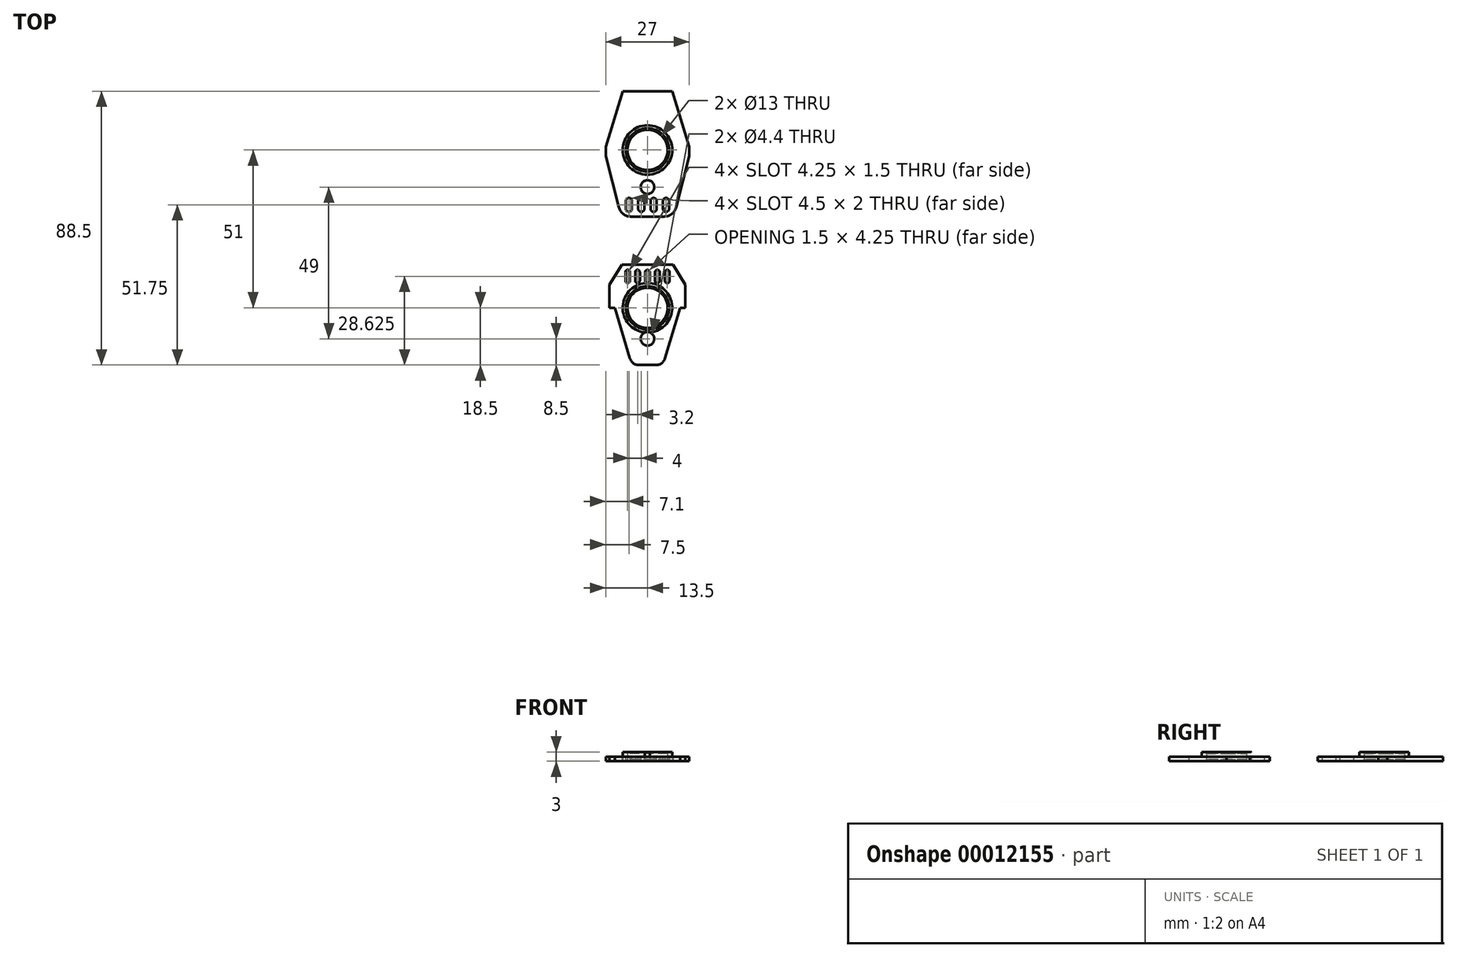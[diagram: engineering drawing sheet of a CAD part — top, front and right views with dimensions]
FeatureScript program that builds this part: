
annotation { "Feature Type Name" : "Feature", "Feature Type Description" : "" }
export const myFeature = defineFeature(function(context is Context, id is Id, definition is map)
    precondition{}
    {
        {
            var Q0;
            Q0=qCreatedBy(makeId("Top.planeOp"),FACE);
            var sketch = newSketch(context, id + "F0", { "sketchPlane" : qUnion([Q0])});
            skLineSegment(sketch, "E0", {"start": v(-13.5, 0) * mm, "end": v(-9.27, -16.5) * mm});
            skLineSegment(sketch, "E1", {"start": v(-5.4, -19.5) * mm, "end": v(0, -19.5) * mm});
            skLineSegment(sketch, "E2", {"start": v(0, -19.5) * mm, "end": v(0, 21) * mm, "construction": true});
            skLineSegment(sketch, "E3", {"start": v(0, 21) * mm, "end": v(-8, 21) * mm});
            skLineSegment(sketch, "E4", {"start": v(-13.5, 0) * mm, "end": v(-13.5, 3) * mm});
            skLineSegment(sketch, "E5", {"start": v(-13.5, 3) * mm, "end": v(-8, 21) * mm});
            skPoint(sketch, "E6.visualSharp", {"position": v(-8.5, -19.5) * mm});
            skArc(sketch, "E6.filletArc", {"start": v(-9.27, -16.5) * mm, "mid": v(-7.85, -18.66) * mm, "end": v(-5.4, -19.5) * mm});
            skLineSegment(sketch, "E7.0.MirrorCS", {"start": v(13.5, 0) * mm, "end": v(13.5, 3) * mm});
            skArc(sketch, "E7.1.MirrorCS", {"start": v(9.27, -16.5) * mm, "mid": v(7.85, -18.66) * mm, "end": v(5.4, -19.5) * mm});
            skPoint(sketch, "E7.2.MirrorP", {"position": v(8.5, -19.5) * mm});
            skLineSegment(sketch, "E7.3.MirrorCS", {"start": v(13.5, 3) * mm, "end": v(8, 21) * mm});
            skLineSegment(sketch, "E7.4.MirrorCS", {"start": v(0, 21) * mm, "end": v(8, 21) * mm});
            skLineSegment(sketch, "E7.5.MirrorCS", {"start": v(13.5, 0) * mm, "end": v(9.27, -16.5) * mm});
            skLineSegment(sketch, "E7.6.MirrorCS", {"start": v(5.4, -19.5) * mm, "end": v(0, -19.5) * mm});
            skSolve(sketch);
        }
        {
            var Q0;
            Q0 = qSketchRegion(id + "F0", true);
            extrude(context, id + "F1", {"entities" : qUnion([Q0]), "depth" : 1.5 * mm});
        }
        {
            var Q0;
            Q0=makeQuery(id+"F1.opExtrude","CAP_FACE",FACE,{"disambiguationData":[OSD([sQuery(id+"F0.wireOp",EDGE,"E0"),sQuery(id+"F0.wireOp",EDGE,"E1"),sQuery(id+"F0.wireOp",EDGE,"E3"),sQuery(id+"F0.wireOp",EDGE,"E4"),sQuery(id+"F0.wireOp",EDGE,"E5"),sQuery(id+"F0.wireOp",EDGE,"E6.filletArc"),sQuery(id+"F0.wireOp",EDGE,"E7.0.MirrorCS"),sQuery(id+"F0.wireOp",EDGE,"E7.1.MirrorCS"),sQuery(id+"F0.wireOp",EDGE,"E7.3.MirrorCS"),sQuery(id+"F0.wireOp",EDGE,"E7.4.MirrorCS"),sQuery(id+"F0.wireOp",EDGE,"E7.5.MirrorCS"),sQuery(id+"F0.wireOp",EDGE,"E7.6.MirrorCS")])],"isStart":false});
            var sketch = newSketch(context, id + "F2", { "sketchPlane" : qUnion([Q0])});
            skCircle(sketch, "E8", {"center": v(0, 2) * mm, "radius": 8 * mm});
            skCircle(sketch, "E9", {"center": v(0, 2) * mm, "radius": 6.5 * mm});
            skSolve(sketch);
        }
        {
            var Q0;
            Q0 = qSketchRegion(id + "F2", true);
            extrude(context, id + "F3", {"entities" : qUnion([Q0]), "operationType" : NewBodyOperationType.ADD, "depth" : 1.5 * mm});
        }
        {
            var Q0;
            Q0=makeQuery(id+"F1.opExtrude","CAP_FACE",FACE,{"disambiguationData":[OSD([sQuery(id+"F0.wireOp",EDGE,"E0"),sQuery(id+"F0.wireOp",EDGE,"E1"),sQuery(id+"F0.wireOp",EDGE,"E3"),sQuery(id+"F0.wireOp",EDGE,"E4"),sQuery(id+"F0.wireOp",EDGE,"E5"),sQuery(id+"F0.wireOp",EDGE,"E6.filletArc"),sQuery(id+"F0.wireOp",EDGE,"E7.0.MirrorCS"),sQuery(id+"F0.wireOp",EDGE,"E7.1.MirrorCS"),sQuery(id+"F0.wireOp",EDGE,"E7.3.MirrorCS"),sQuery(id+"F0.wireOp",EDGE,"E7.4.MirrorCS"),sQuery(id+"F0.wireOp",EDGE,"E7.5.MirrorCS"),sQuery(id+"F0.wireOp",EDGE,"E7.6.MirrorCS")])],"isStart":false});
            var sketch = newSketch(context, id + "F4", { "sketchPlane" : qUnion([Q0])});
            skCircle(sketch, "E10", {"center": v(0, 2) * mm, "radius": 6.5 * mm});
            skCircle(sketch, "E11", {"center": v(0, -10) * mm, "radius": 2.2 * mm});
            skLineSegment(sketch, "E12", {"start": v(-7, -14.5) * mm, "end": v(-7, -17) * mm});
            skArc(sketch, "E13", {"start": v(-7, -17) * mm, "mid": v(-6, -18) * mm, "end": v(-5, -17) * mm});
            skLineSegment(sketch, "E14", {"start": v(-5, -17) * mm, "end": v(-5, -14.5) * mm});
            skArc(sketch, "E15", {"start": v(-5, -14.5) * mm, "mid": v(-6, -13.5) * mm, "end": v(-7, -14.5) * mm});
            skArc(sketch, "E16.1.0.0", {"start": v(-3, -17) * mm, "mid": v(-2, -18) * mm, "end": v(-1, -17) * mm});
            skLineSegment(sketch, "E16.1.0.1", {"start": v(-1, -17) * mm, "end": v(-1, -14.5) * mm});
            skArc(sketch, "E16.1.0.2", {"start": v(-1, -14.5) * mm, "mid": v(-2, -13.5) * mm, "end": v(-3, -14.5) * mm});
            skLineSegment(sketch, "E16.1.0.3", {"start": v(-3, -14.5) * mm, "end": v(-3, -17) * mm});
            skArc(sketch, "E16.2.0.0", {"start": v(1, -17) * mm, "mid": v(2, -18) * mm, "end": v(3, -17) * mm});
            skLineSegment(sketch, "E16.2.0.1", {"start": v(3, -17) * mm, "end": v(3, -14.5) * mm});
            skArc(sketch, "E16.2.0.2", {"start": v(3, -14.5) * mm, "mid": v(2, -13.5) * mm, "end": v(1, -14.5) * mm});
            skLineSegment(sketch, "E16.2.0.3", {"start": v(1, -14.5) * mm, "end": v(1, -17) * mm});
            skArc(sketch, "E16.3.0.0", {"start": v(5, -17) * mm, "mid": v(6, -18) * mm, "end": v(7, -17) * mm});
            skLineSegment(sketch, "E16.3.0.1", {"start": v(7, -17) * mm, "end": v(7, -14.5) * mm});
            skArc(sketch, "E16.3.0.2", {"start": v(7, -14.5) * mm, "mid": v(6, -13.5) * mm, "end": v(5, -14.5) * mm});
            skLineSegment(sketch, "E16.3.0.3", {"start": v(5, -14.5) * mm, "end": v(5, -17) * mm});
            skLineSegment(sketch, "E16.direction1", {"start": v(-7, -17) * mm, "end": v(-3, -17) * mm, "construction": true});
            skSolve(sketch);
        }
        {
            var Q0;
            Q0 = qSketchRegion(id + "F4", true);
            extrude(context, id + "F5", {"entities" : qUnion([Q0]), "operationType" : NewBodyOperationType.REMOVE, "endBound" : BoundingType.THROUGH_ALL, "oppositeDirection" : true, "depth" : 25 * mm});
        }
        {
            var Q0;
            Q0=qCreatedBy(makeId("Top.planeOp"),FACE);
            var sketch = newSketch(context, id + "F6", { "sketchPlane" : qUnion([Q0])});
            skLineSegment(sketch, "E17", {"start": v(0, -35) * mm, "end": v(0, -67.5) * mm, "construction": true});
            skLineSegment(sketch, "E18", {"start": v(0, -67.5) * mm, "end": v(-2.76, -67.5) * mm});
            skLineSegment(sketch, "E19", {"start": v(-5.64, -65.35) * mm, "end": v(-10.5, -49) * mm});
            skLineSegment(sketch, "E20", {"start": v(-10.5, -49) * mm, "end": v(-12.25, -49) * mm});
            skLineSegment(sketch, "E21", {"start": v(-12.25, -49) * mm, "end": v(-12.25, -41.5) * mm});
            skLineSegment(sketch, "E22", {"start": v(-12.25, -41.5) * mm, "end": v(-8.25, -35) * mm});
            skLineSegment(sketch, "E23", {"start": v(-8.25, -35) * mm, "end": v(0, -35) * mm});
            skPoint(sketch, "E24.visualSharp", {"position": v(-5, -67.5) * mm});
            skArc(sketch, "E24.filletArc", {"start": v(-5.64, -65.35) * mm, "mid": v(-4.56, -66.9) * mm, "end": v(-2.76, -67.5) * mm});
            skLineSegment(sketch, "E25.0.MirrorCS", {"start": v(12.25, -41.5) * mm, "end": v(8.25, -35) * mm});
            skLineSegment(sketch, "E25.1.MirrorCS", {"start": v(12.25, -49) * mm, "end": v(12.25, -41.5) * mm});
            skLineSegment(sketch, "E25.2.MirrorCS", {"start": v(0, -67.5) * mm, "end": v(2.76, -67.5) * mm});
            skPoint(sketch, "E25.3.MirrorP", {"position": v(5, -67.5) * mm});
            skLineSegment(sketch, "E25.4.MirrorCS", {"start": v(10.5, -49) * mm, "end": v(12.25, -49) * mm});
            skArc(sketch, "E25.5.MirrorCS", {"start": v(5.64, -65.35) * mm, "mid": v(4.56, -66.9) * mm, "end": v(2.76, -67.5) * mm});
            skLineSegment(sketch, "E25.6.MirrorCS", {"start": v(5.64, -65.35) * mm, "end": v(10.5, -49) * mm});
            skLineSegment(sketch, "E25.7.MirrorCS", {"start": v(8.25, -35) * mm, "end": v(0, -35) * mm});
            skSolve(sketch);
        }
        {
            var Q0;
            Q0 = qSketchRegion(id + "F6", true);
            extrude(context, id + "F7", {"entities" : qUnion([Q0]), "depth" : 1.5 * mm});
        }
        {
            var Q0;
            Q0=makeQuery(id+"F7.opExtrude","CAP_FACE",FACE,{"disambiguationData":[OSD([sQuery(id+"F6.wireOp",EDGE,"E18"),sQuery(id+"F6.wireOp",EDGE,"E19"),sQuery(id+"F6.wireOp",EDGE,"E20"),sQuery(id+"F6.wireOp",EDGE,"E21"),sQuery(id+"F6.wireOp",EDGE,"E22"),sQuery(id+"F6.wireOp",EDGE,"E23"),sQuery(id+"F6.wireOp",EDGE,"E24.filletArc"),sQuery(id+"F6.wireOp",EDGE,"E25.0.MirrorCS"),sQuery(id+"F6.wireOp",EDGE,"E25.1.MirrorCS"),sQuery(id+"F6.wireOp",EDGE,"E25.2.MirrorCS"),sQuery(id+"F6.wireOp",EDGE,"E25.4.MirrorCS"),sQuery(id+"F6.wireOp",EDGE,"E25.5.MirrorCS"),sQuery(id+"F6.wireOp",EDGE,"E25.6.MirrorCS"),sQuery(id+"F6.wireOp",EDGE,"E25.7.MirrorCS")])],"isStart":false});
            var sketch = newSketch(context, id + "F8", { "sketchPlane" : qUnion([Q0])});
            skCircle(sketch, "E26", {"center": v(0, -49) * mm, "radius": 6.5 * mm});
            skCircle(sketch, "E27", {"center": v(0, -49) * mm, "radius": 8 * mm});
            skSolve(sketch);
        }
        {
            var Q0;
            Q0 = qSketchRegion(id + "F8", true);
            extrude(context, id + "F9", {"entities" : qUnion([Q0]), "operationType" : NewBodyOperationType.ADD, "depth" : 1.5 * mm});
        }
        {
            var Q0;
            Q0=makeQuery(id+"F9.boolean.opBoolean","SPLIT",FACE,{"disambiguationData":[TD([makeQuery(id+"F9.opExtrude","SWEPT_FACE",FACE,{"disambiguationData":[OSD([sQuery(id+"F8.wireOp",EDGE,"E26")])]})])],"derivedFrom":makeQuery(id+"F7.opExtrude","CAP_FACE",FACE,{"disambiguationData":[OSD([sQuery(id+"F6.wireOp",EDGE,"E18"),sQuery(id+"F6.wireOp",EDGE,"E19"),sQuery(id+"F6.wireOp",EDGE,"E20"),sQuery(id+"F6.wireOp",EDGE,"E21"),sQuery(id+"F6.wireOp",EDGE,"E22"),sQuery(id+"F6.wireOp",EDGE,"E23"),sQuery(id+"F6.wireOp",EDGE,"E24.filletArc"),sQuery(id+"F6.wireOp",EDGE,"E25.0.MirrorCS"),sQuery(id+"F6.wireOp",EDGE,"E25.1.MirrorCS"),sQuery(id+"F6.wireOp",EDGE,"E25.2.MirrorCS"),sQuery(id+"F6.wireOp",EDGE,"E25.4.MirrorCS"),sQuery(id+"F6.wireOp",EDGE,"E25.5.MirrorCS"),sQuery(id+"F6.wireOp",EDGE,"E25.6.MirrorCS"),sQuery(id+"F6.wireOp",EDGE,"E25.7.MirrorCS")])],"isStart":false})});
            var sketch = newSketch(context, id + "F10", { "sketchPlane" : qUnion([Q0])});
            skCircle(sketch, "E28", {"center": v(0, -49) * mm, "radius": 6.5 * mm});
            skSolve(sketch);
        }
        {
            var Q0;
            Q0 = qSketchRegion(id + "F10", true);
            extrude(context, id + "F11", {"entities" : qUnion([Q0]), "operationType" : NewBodyOperationType.REMOVE, "endBound" : BoundingType.THROUGH_ALL, "oppositeDirection" : true, "depth" : 25 * mm});
        }
        {
            var Q0;
            {var subQ0=sQuery(id+"F6.wireOp",EDGE,"E18");var subQ1=sQuery(id+"F6.wireOp",EDGE,"E19");var subQ2=sQuery(id+"F6.wireOp",EDGE,"E20");var subQ3=sQuery(id+"F6.wireOp",EDGE,"E21");var subQ4=sQuery(id+"F6.wireOp",EDGE,"E22");var subQ5=sQuery(id+"F6.wireOp",EDGE,"E23");var subQ6=sQuery(id+"F6.wireOp",EDGE,"E24.filletArc");var subQ7=sQuery(id+"F6.wireOp",EDGE,"E25.0.MirrorCS");var subQ8=sQuery(id+"F6.wireOp",EDGE,"E25.1.MirrorCS");var subQ9=sQuery(id+"F6.wireOp",EDGE,"E25.2.MirrorCS");var subQ10=sQuery(id+"F6.wireOp",EDGE,"E25.4.MirrorCS");var subQ11=sQuery(id+"F6.wireOp",EDGE,"E25.5.MirrorCS");var subQ12=sQuery(id+"F6.wireOp",EDGE,"E25.6.MirrorCS");var subQ13=sQuery(id+"F6.wireOp",EDGE,"E25.7.MirrorCS");Q0=makeQuery(id+"F9.boolean.opBoolean","SPLIT",FACE,{"disambiguationData":[TD([makeQuery(id+"F7.opExtrude","SWEPT_FACE",FACE,{"disambiguationData":[OSD([subQ1])]})])],"derivedFrom":makeQuery(id+"F7.opExtrude","CAP_FACE",FACE,{"disambiguationData":[OSD([subQ0,subQ1,subQ2,subQ3,subQ4,subQ5,subQ6,subQ7,subQ8,subQ9,subQ10,subQ11,subQ12,subQ13])],"isStart":false})});}
            var sketch = newSketch(context, id + "F12", { "sketchPlane" : qUnion([Q0])});
            skLineSegment(sketch, "E29", {"start": v(-0.75, -37.5) * mm, "end": v(-0.75, -40.25) * mm});
            skArc(sketch, "E30", {"start": v(-0.75, -40.25) * mm, "mid": v(0, -41) * mm, "end": v(0.75, -40.25) * mm});
            skLineSegment(sketch, "E31", {"start": v(0.75, -40.25) * mm, "end": v(0.75, -37.5) * mm});
            skArc(sketch, "E32", {"start": v(0.75, -37.5) * mm, "mid": v(0, -36.75) * mm, "end": v(-0.75, -37.5) * mm});
            skArc(sketch, "E33.1.0.0", {"start": v(3.95, -37.5) * mm, "mid": v(3.2, -36.75) * mm, "end": v(2.45, -37.5) * mm});
            skLineSegment(sketch, "E33.1.0.1", {"start": v(3.95, -40.25) * mm, "end": v(3.95, -37.5) * mm});
            skLineSegment(sketch, "E33.1.0.2", {"start": v(2.45, -37.5) * mm, "end": v(2.45, -40.25) * mm});
            skArc(sketch, "E33.1.0.3", {"start": v(2.45, -40.25) * mm, "mid": v(3.2, -41) * mm, "end": v(3.95, -40.25) * mm});
            skArc(sketch, "E33.2.0.0", {"start": v(7.15, -37.5) * mm, "mid": v(6.4, -36.75) * mm, "end": v(5.65, -37.5) * mm});
            skLineSegment(sketch, "E33.2.0.1", {"start": v(7.15, -40.25) * mm, "end": v(7.15, -37.5) * mm});
            skLineSegment(sketch, "E33.2.0.2", {"start": v(5.65, -37.5) * mm, "end": v(5.65, -40.25) * mm});
            skArc(sketch, "E33.2.0.3", {"start": v(5.65, -40.25) * mm, "mid": v(6.4, -41) * mm, "end": v(7.15, -40.25) * mm});
            skLineSegment(sketch, "E33.direction1", {"start": v(-0.75, -37.5) * mm, "end": v(2.45, -37.5) * mm, "construction": true});
            skArc(sketch, "E34.1.0.0", {"start": v(-3.95, -40.25) * mm, "mid": v(-3.2, -41) * mm, "end": v(-2.45, -40.25) * mm});
            skLineSegment(sketch, "E34.1.0.1", {"start": v(-3.95, -37.5) * mm, "end": v(-3.95, -40.25) * mm});
            skArc(sketch, "E34.1.0.2", {"start": v(-2.45, -37.5) * mm, "mid": v(-3.2, -36.75) * mm, "end": v(-3.95, -37.5) * mm});
            skLineSegment(sketch, "E34.1.0.3", {"start": v(-2.45, -40.25) * mm, "end": v(-2.45, -37.5) * mm});
            skArc(sketch, "E34.2.0.0", {"start": v(-7.15, -40.25) * mm, "mid": v(-6.4, -41) * mm, "end": v(-5.65, -40.25) * mm});
            skLineSegment(sketch, "E34.2.0.1", {"start": v(-7.15, -37.5) * mm, "end": v(-7.15, -40.25) * mm});
            skArc(sketch, "E34.2.0.2", {"start": v(-5.65, -37.5) * mm, "mid": v(-6.4, -36.75) * mm, "end": v(-7.15, -37.5) * mm});
            skLineSegment(sketch, "E34.2.0.3", {"start": v(-5.65, -40.25) * mm, "end": v(-5.65, -37.5) * mm});
            skLineSegment(sketch, "E34.direction1", {"start": v(-0.75, -40.25) * mm, "end": v(-3.95, -40.25) * mm, "construction": true});
            skCircle(sketch, "E35", {"center": v(0, -59) * mm, "radius": 2.2 * mm});
            skSolve(sketch);
        }
        {
            var Q0;
            Q0 = qSketchRegion(id + "F12", true);
            extrude(context, id + "F13", {"entities" : qUnion([Q0]), "operationType" : NewBodyOperationType.REMOVE, "endBound" : BoundingType.THROUGH_ALL, "depth" : 25 * mm, "hasSecondDirection" : true, "secondDirectionBound" : SecondDirectionBoundingType.THROUGH_ALL, "secondDirectionOppositeDirection" : true, "secondDirectionDepth" : 25 * mm});
        }
        {
            var Q0;
            Q0=makeQuery(id+"F3.opExtrude","CAP_EDGE",EDGE,{"disambiguationData":[OSD([sQuery(id+"F2.wireOp",EDGE,"E9")])],"isStart":false});
            var Q1;
            Q1=makeQuery(id+"F5.boolean.opBoolean","INTERSECT",EDGE,{"derivedFrom":[makeQuery(id+"F1.opExtrude","CAP_FACE",FACE,{"disambiguationData":[OSD([sQuery(id+"F0.wireOp",EDGE,"E0"),sQuery(id+"F0.wireOp",EDGE,"E1"),sQuery(id+"F0.wireOp",EDGE,"E3"),sQuery(id+"F0.wireOp",EDGE,"E4"),sQuery(id+"F0.wireOp",EDGE,"E5"),sQuery(id+"F0.wireOp",EDGE,"E6.filletArc"),sQuery(id+"F0.wireOp",EDGE,"E7.0.MirrorCS"),sQuery(id+"F0.wireOp",EDGE,"E7.1.MirrorCS"),sQuery(id+"F0.wireOp",EDGE,"E7.3.MirrorCS"),sQuery(id+"F0.wireOp",EDGE,"E7.4.MirrorCS"),sQuery(id+"F0.wireOp",EDGE,"E7.5.MirrorCS"),sQuery(id+"F0.wireOp",EDGE,"E7.6.MirrorCS")])],"isStart":true}),makeQuery(id+"F5.opExtrude","SWEPT_FACE",FACE,{"disambiguationData":[OSD([sQuery(id+"F4.wireOp",EDGE,"E10")])]})]});
            var Q2;
            Q2=makeQuery(id+"F9.opExtrude","CAP_EDGE",EDGE,{"disambiguationData":[OSD([sQuery(id+"F8.wireOp",EDGE,"E26")])],"isStart":false});
            var Q3;
            Q3=makeQuery(id+"F11.boolean.opBoolean","INTERSECT",EDGE,{"derivedFrom":[makeQuery(id+"F7.opExtrude","CAP_FACE",FACE,{"disambiguationData":[OSD([sQuery(id+"F6.wireOp",EDGE,"E18"),sQuery(id+"F6.wireOp",EDGE,"E19"),sQuery(id+"F6.wireOp",EDGE,"E20"),sQuery(id+"F6.wireOp",EDGE,"E21"),sQuery(id+"F6.wireOp",EDGE,"E22"),sQuery(id+"F6.wireOp",EDGE,"E23"),sQuery(id+"F6.wireOp",EDGE,"E24.filletArc"),sQuery(id+"F6.wireOp",EDGE,"E25.0.MirrorCS"),sQuery(id+"F6.wireOp",EDGE,"E25.1.MirrorCS"),sQuery(id+"F6.wireOp",EDGE,"E25.2.MirrorCS"),sQuery(id+"F6.wireOp",EDGE,"E25.4.MirrorCS"),sQuery(id+"F6.wireOp",EDGE,"E25.5.MirrorCS"),sQuery(id+"F6.wireOp",EDGE,"E25.6.MirrorCS"),sQuery(id+"F6.wireOp",EDGE,"E25.7.MirrorCS")])],"isStart":true}),makeQuery(id+"F11.opExtrude","SWEPT_FACE",FACE,{"disambiguationData":[OSD([sQuery(id+"F10.wireOp",EDGE,"E28")])]})]});
            chamfer(context, id + "F14", {"entities" : qUnion([Q0, Q1, Q2, Q3]), "width" : 0.5 * mm, "tangentPropagation" : true});
        }
    });
